# Revit family: PFX_A3-Toilet-Cubicle-Assembly
name_source: partatom
category: Generic Models
revit_build: Autodesk Revit 2016 (Build: 20150220_1215(x64)
units: mm (PartAtom-declared; Revit-internal decimal feet)

## family parameters
Always vertical = Yes
Can host rebar = No
Cut with Voids When Loaded = No
Host = Wall
Part Type = Undefined
Room Calculation Point = No
Round Connector Dimension = Use Diameter
Shared = No

## types (2) — shared parameters
Bttm Frame Depth = 45 mm  [stored 0.147638 ft]
Cubicle Base Offset = 150 mm  [stored 0.492126 ft]
Cubicle Clear Width = 800 mm  [stored 2.62467 ft]
Cubicle Height = 1800 mm  [stored 5.90551 ft]
Cubicle Length = 1500 mm  [stored 4.92126 ft]
Cubicle Panel Thickness = 20 mm  [stored 0.0656168 ft]
Cubicle Width = 820 mm  [stored 2.69029 ft]
Door Head Clearance = 10 mm  [stored 0.0328084 ft]
Handle Mounting Height = 800 mm  [stored 2.62467 ft]
Keynote = K32
Material Cubicle Framing = Toilet Cubicle Frame
Material Cubicle Panel = Toilet Cubicle Panelling
Material Feet = Toilet Cubicle Feet
Material Ironmongery = Metal - Aluminium
Top Frame Depth = 45 mm  [stored 0.147638 ft]

## per-type parameters (varying)
| type | No of Mid Cubicles | Terraced Length |
| Cubicles - Min 4No | 2 | 2460 mm |
| Cubicles - 6 No | 4 | 4100 mm  [stored 13.4514 ft] |

note: [stored X ft] marks values corroborated as IEEE doubles in the binary element streams (Revit-internal decimal feet)

## geometry (parser evidence)
native form markers: Sweep x33
no freeform markers — native parametric forms only
